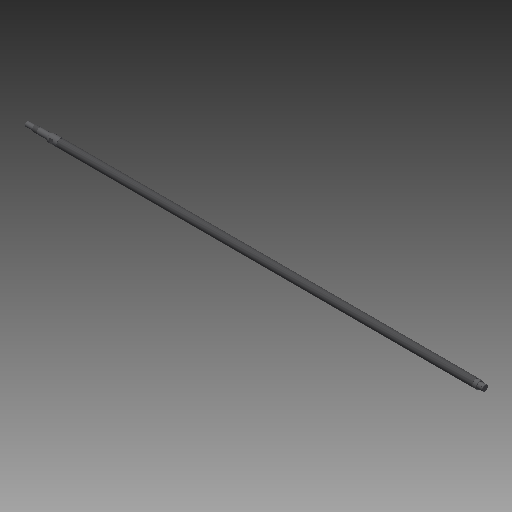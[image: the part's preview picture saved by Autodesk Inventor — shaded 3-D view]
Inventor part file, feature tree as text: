
AUTODESK INVENTOR PART (.ipt)
format: ipt  version: 2018 (Build 220112000, 112)  size: 146,432 bytes
history: native  units: mm
features: other x21, sketch x5, revolve x3, thread x2, extrude x2
ambient origin geometry x8: Origin, YZ Plane, XZ Plane, XY Plane, X Axis, Y Axis, Z Axis, Center Point
bodies: Solid1 (feature_tree)
feature tree (33):
  revolve  "Revolution1"  [1 undecoded]
  thread  "Thread1"  [1 undecoded]
  revolve  "Revolution2"  [1 undecoded]
  thread  "Thread2"  [1 undecoded]
  extrude  "Extrusion1"  TaperAngle=0.0deg  [1 undecoded]
  extrude  "Extrusion2"  [1 undecoded]
  revolve  "Revolution3"  [1 undecoded]
  other  "FSS_XY"
  other  "FSS_YZ"
  other  "FSS_ZX"
  other  "FSS_X"
  other  "FSS_Y"
  other  "FSS_Z"
  other  "FSS_Center"
  other  "SSS_XY"
  other  "SSS_YZ"
  other  "SSS_ZX"
  other  "SSS_X"
  other  "SSS_Y"
  other  "SSS_Z"
  other  "SSS_Center"
  other  "bnt_s_1_XY"
  other  "bnt_s_1_YZ"
  other  "bnt_s_1_ZX"
  other  "bnt_s_1_X"
  other  "bnt_s_1_Y"
  other  "bnt_s_1_Z"
  other  "bnt_s_1_Center"
  sketch  "Sketch_1"  dims[d0=360.0deg d1=1058.0mm d2=0.0mm d3=360.0deg]
  sketch  "Sketch_10"  dims[d4=11.3865mm d5=0.0mm d6=4.0mm d7=0.0mm d8=4.0mm d9=0.0mm]
  sketch  "Sketch_11"  dims[d10=360.0deg d11=0.0mm d12=0.0mm d13=0.0mm]
  sketch  "Sketch_12"
  sketch  "Sketch_16"
note: 7 required parameter values undecoded (feature->parameter linkage not recoverable at this tier; creation-order binding heuristic only, values carry confidence <= 0.55)